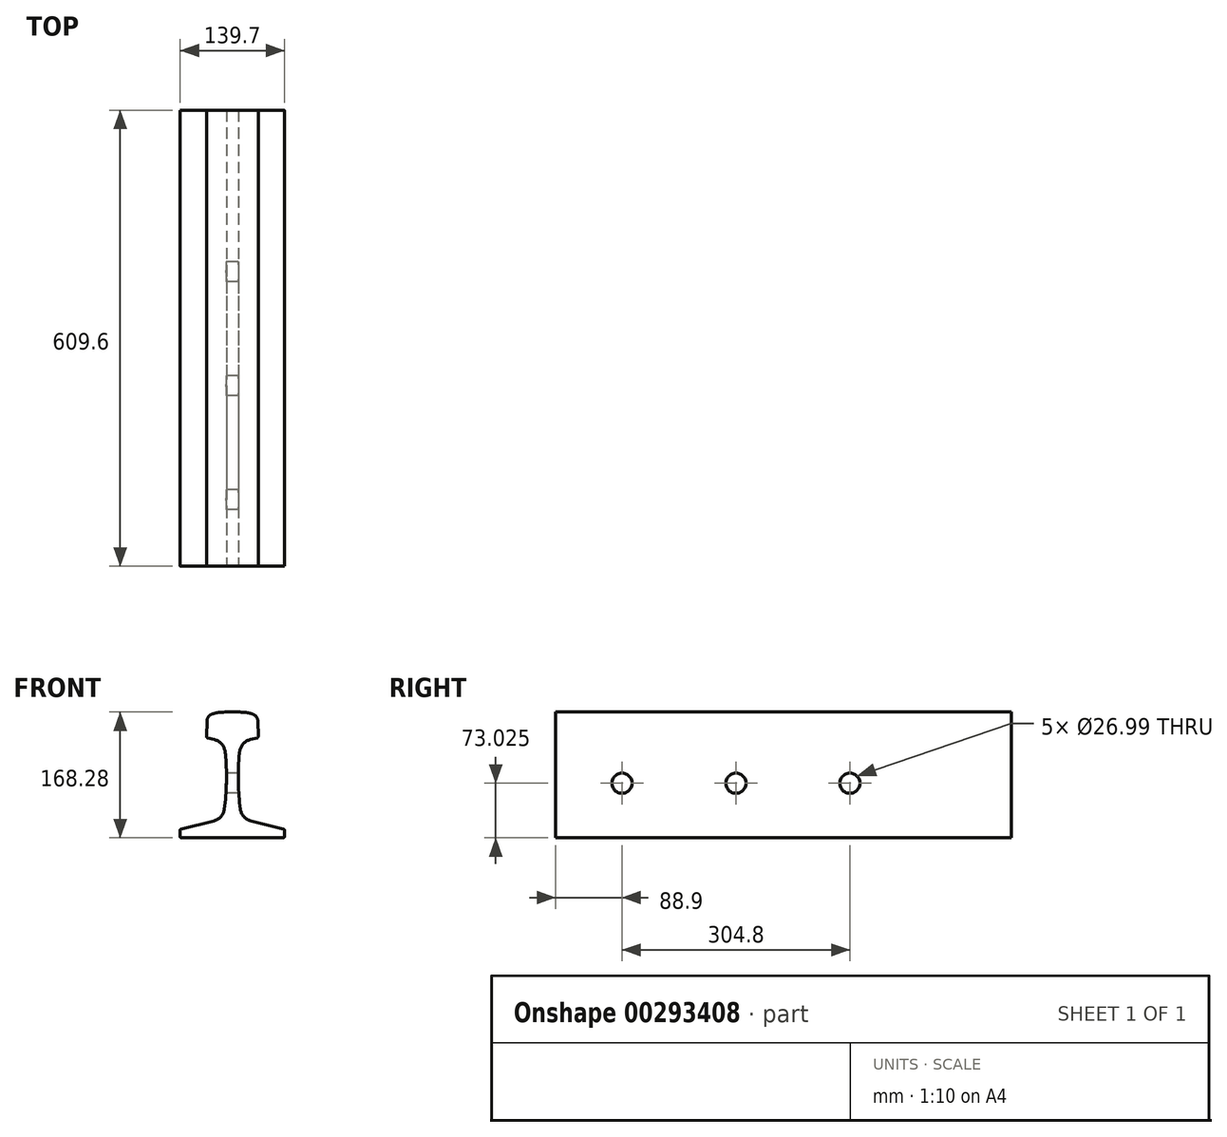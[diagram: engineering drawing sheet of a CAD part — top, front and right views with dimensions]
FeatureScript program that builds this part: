
annotation { "Feature Type Name" : "Feature", "Feature Type Description" : "" }
export const myFeature = defineFeature(function(context is Context, id is Id, definition is map)
    precondition{}
    {
        {
            var Q0;
            Q0=qCreatedBy(makeId("Front.planeOp"),FACE);
            var sketch = newSketch(context, id + "F0", { "sketchPlane" : qUnion([Q0])});
            skLineSegment(sketch, "E0", {"start": v(0, 192.8) * mm, "end": v(0, -23.67) * mm, "construction": true});
            skLineSegment(sketch, "E1", {"start": v(0, 0) * mm, "end": v(68.26, 0) * mm});
            skLineSegment(sketch, "E2", {"start": v(69.85, 1.59) * mm, "end": v(69.85, 9.92) * mm});
            skLineSegment(sketch, "E3", {"start": v(68.65, 11.46) * mm, "end": v(24.97, 22.35) * mm});
            skArc(sketch, "E4", {"start": v(68.26, 0) * mm, "mid": v(69.39, 0.46) * mm, "end": v(69.85, 1.59) * mm});
            skArc(sketch, "E5", {"start": v(69.85, 9.92) * mm, "mid": v(69.51, 10.9) * mm, "end": v(68.65, 11.46) * mm});
            skArc(sketch, "E6", {"start": v(10.68, 38.47) * mm, "mid": v(15.33, 28.2) * mm, "end": v(24.97, 22.35) * mm});
            skArc(sketch, "E7", {"start": v(7.94, 82.55) * mm, "mid": v(8.62, 60.47) * mm, "end": v(10.68, 38.47) * mm});
            skArc(sketch, "E8", {"start": v(8.85, 107.95) * mm, "mid": v(8.16, 95.26) * mm, "end": v(7.94, 82.55) * mm});
            skLineSegment(sketch, "E9", {"start": v(-374.2, 82.55) * mm, "end": v(-11.1, 82.55) * mm, "construction": true});
            skArc(sketch, "E10", {"start": v(9.93, 116.4) * mm, "mid": v(9.27, 112.19) * mm, "end": v(8.85, 107.95) * mm});
            skLineSegment(sketch, "E11", {"start": v(-63.11, 125.41) * mm, "end": v(54.14, 125.41) * mm, "construction": true});
            skArc(sketch, "E12", {"start": v(15.87, 167.78) * mm, "mid": v(7.94, 168.15) * mm, "end": v(0, 168.28) * mm});
            skArc(sketch, "E13", {"start": v(28.14, 164.93) * mm, "mid": v(22.13, 166.86) * mm, "end": v(15.87, 167.78) * mm});
            skArc(sketch, "E14", {"start": v(34, 156.37) * mm, "mid": v(32.34, 161.52) * mm, "end": v(28.14, 164.93) * mm});
            skArc(sketch, "E15", {"start": v(33.32, 133.72) * mm, "mid": v(34.2, 134.3) * mm, "end": v(34.53, 135.3) * mm});
            skLineSegment(sketch, "E16", {"start": v(34, 156.37) * mm, "end": v(34.53, 135.3) * mm});
            skArc(sketch, "E17", {"start": v(24.05, 131.4) * mm, "mid": v(14.78, 125.98) * mm, "end": v(9.93, 116.4) * mm});
            skLineSegment(sketch, "E18", {"start": v(24.05, 131.4) * mm, "end": v(33.32, 133.72) * mm});
            skLineSegment(sketch, "E19", {"start": v(34.53, 172.82) * mm, "end": v(34.53, 129.5) * mm, "construction": true});
            skArc(sketch, "E20.MirrorCS", {"start": v(-68.26, 0) * mm, "mid": v(-69.39, 0.46) * mm, "end": v(-69.85, 1.59) * mm});
            skLineSegment(sketch, "E21.MirrorCS", {"start": v(0, 0) * mm, "end": v(-68.26, 0) * mm});
            skLineSegment(sketch, "E22.MirrorCS", {"start": v(-69.85, 1.59) * mm, "end": v(-69.85, 9.92) * mm});
            skArc(sketch, "E23.MirrorCS", {"start": v(-69.85, 9.92) * mm, "mid": v(-69.51, 10.9) * mm, "end": v(-68.65, 11.46) * mm});
            skLineSegment(sketch, "E24.MirrorCS", {"start": v(-68.65, 11.46) * mm, "end": v(-24.97, 22.35) * mm});
            skArc(sketch, "E25.MirrorCS", {"start": v(-10.68, 38.47) * mm, "mid": v(-15.33, 28.2) * mm, "end": v(-24.97, 22.35) * mm});
            skArc(sketch, "E26.MirrorCS", {"start": v(-7.94, 82.55) * mm, "mid": v(-8.62, 60.47) * mm, "end": v(-10.68, 38.47) * mm});
            skArc(sketch, "E27.MirrorCS", {"start": v(-8.85, 107.95) * mm, "mid": v(-8.16, 95.26) * mm, "end": v(-7.94, 82.55) * mm});
            skArc(sketch, "E28.MirrorCS", {"start": v(-9.93, 116.4) * mm, "mid": v(-9.27, 112.19) * mm, "end": v(-8.85, 107.95) * mm});
            skArc(sketch, "E29.MirrorCS", {"start": v(-24.05, 131.4) * mm, "mid": v(-14.78, 125.98) * mm, "end": v(-9.93, 116.4) * mm});
            skLineSegment(sketch, "E30.MirrorCS", {"start": v(-34, 156.37) * mm, "end": v(-34.53, 135.3) * mm});
            skLineSegment(sketch, "E31.MirrorCS", {"start": v(-24.05, 131.4) * mm, "end": v(-33.32, 133.72) * mm});
            skArc(sketch, "E32.MirrorCS", {"start": v(-33.32, 133.72) * mm, "mid": v(-34.2, 134.3) * mm, "end": v(-34.53, 135.3) * mm});
            skArc(sketch, "E33.MirrorCS", {"start": v(-34, 156.37) * mm, "mid": v(-32.34, 161.52) * mm, "end": v(-28.14, 164.93) * mm});
            skArc(sketch, "E34.MirrorCS", {"start": v(-28.14, 164.93) * mm, "mid": v(-22.13, 166.86) * mm, "end": v(-15.87, 167.78) * mm});
            skArc(sketch, "E35.MirrorCS", {"start": v(-15.88, 167.78) * mm, "mid": v(-7.94, 168.15) * mm, "end": v(0, 168.28) * mm});
            skLineSegment(sketch, "E36", {"start": v(0, 28.57) * mm, "end": v(-68.65, 11.46) * mm, "construction": true});
            skLineSegment(sketch, "E37", {"start": v(-54.52, 28.57) * mm, "end": v(0, 28.57) * mm, "construction": true});
            skLineSegment(sketch, "E38", {"start": v(-34.53, 173.1) * mm, "end": v(-34.53, 129.66) * mm, "construction": true});
            skLineSegment(sketch, "E39", {"start": v(0, 125.41) * mm, "end": v(-57.31, 139.7) * mm, "construction": true});
            skLineSegment(sketch, "E40", {"start": v(-24.48, 73.03) * mm, "end": v(98.37, 73.03) * mm, "construction": true});
            skPoint(sketch, "E41", {"position": v(8.07, 73.03) * mm});
            skPoint(sketch, "E42", {"position": v(-8.07, 73.03) * mm});
            skSolve(sketch);
        }
        {
            var Q0;
            Q0=makeQuery(id+"F0.imprint","IMPRINT",FACE,{"disambiguationData":[TD([[makeQuery(id+"F0.imprint","IMPRINT",EDGE,{"derivedFrom":sQuery(id+"F0.wireOp",EDGE,"E1")}),1.0]])]});
            extrude(context, id + "F1", {"entities" : qUnion([Q0]), "oppositeDirection" : true, "depth" : 609.6 * mm});
        }
        {
            var Q0;
            Q0=qCreatedBy(makeId("Right.planeOp"),FACE);
            cPlane(context, id + "F2", {"entities" : qUnion([Q0]), "cplaneType" : CPlaneType.OFFSET, "offset" : 76.2 * mm, "width" : 152.4 * mm, "height" : 152.4 * mm});
        }
        {
            var Q0;
            Q0=qCreatedBy(id+"F2.planeOp",FACE);
            var sketch = newSketch(context, id + "F3", { "sketchPlane" : qUnion([Q0])});
            skPoint(sketch, "E43", {"position": v(88.9, 73.02) * mm});
            skPoint(sketch, "E44", {"position": v(241.3, 73.03) * mm});
            skPoint(sketch, "E45", {"position": v(393.7, 73.03) * mm});
            skLineSegment(sketch, "E46", {"start": v(-1.59, 181.23) * mm, "end": v(-1.59, -28.23) * mm, "construction": true});
            skPoint(sketch, "E47.MirrorP", {"position": v(-396.88, 73.02) * mm});
            skPoint(sketch, "E48.MirrorP", {"position": v(-244.48, 73.02) * mm});
            skPoint(sketch, "E49.MirrorP", {"position": v(-92.08, 73.02) * mm});
            skSolve(sketch);
        }
        {
            var Q0;
            Q0=makeQuery(id+"F0.imprint","IMPRINT",FACE,{"disambiguationData":[TD([[makeQuery(id+"F0.imprint","IMPRINT",EDGE,{"derivedFrom":sQuery(id+"F0.wireOp",EDGE,"E1")}),1.0]])]});
            extrude(context, id + "F4", {"entities" : qUnion([Q0]), "oppositeDirection" : true, "depth" : 609.6 * mm});
        }
        {
            var Q0;
            Q0=sQuery(id+"F3.wireOp",VERTEX,"E43");
            var Q1;
            Q1=sQuery(id+"F3.wireOp",VERTEX,"E44");
            var Q2;
            Q2=makeQuery(id+"F4.opExtrude","SWEPT_BODY",BODY,{"disambiguationData":[OSD([sQuery(id+"F0.wireOp",EDGE,"E1"),sQuery(id+"F0.wireOp",EDGE,"E2"),sQuery(id+"F0.wireOp",EDGE,"E3"),sQuery(id+"F0.wireOp",EDGE,"E4"),sQuery(id+"F0.wireOp",EDGE,"E5"),sQuery(id+"F0.wireOp",EDGE,"E6"),sQuery(id+"F0.wireOp",EDGE,"E7"),sQuery(id+"F0.wireOp",EDGE,"E8"),sQuery(id+"F0.wireOp",EDGE,"E10"),sQuery(id+"F0.wireOp",EDGE,"E12"),sQuery(id+"F0.wireOp",EDGE,"E13"),sQuery(id+"F0.wireOp",EDGE,"E14"),sQuery(id+"F0.wireOp",EDGE,"E15"),sQuery(id+"F0.wireOp",EDGE,"E16"),sQuery(id+"F0.wireOp",EDGE,"E17"),sQuery(id+"F0.wireOp",EDGE,"E18"),sQuery(id+"F0.wireOp",EDGE,"E20.MirrorCS"),sQuery(id+"F0.wireOp",EDGE,"E21.MirrorCS"),sQuery(id+"F0.wireOp",EDGE,"E22.MirrorCS"),sQuery(id+"F0.wireOp",EDGE,"E23.MirrorCS"),sQuery(id+"F0.wireOp",EDGE,"E24.MirrorCS"),sQuery(id+"F0.wireOp",EDGE,"E25.MirrorCS"),sQuery(id+"F0.wireOp",EDGE,"E26.MirrorCS"),sQuery(id+"F0.wireOp",EDGE,"E27.MirrorCS"),sQuery(id+"F0.wireOp",EDGE,"E28.MirrorCS"),sQuery(id+"F0.wireOp",EDGE,"E29.MirrorCS"),sQuery(id+"F0.wireOp",EDGE,"E30.MirrorCS"),sQuery(id+"F0.wireOp",EDGE,"E31.MirrorCS"),sQuery(id+"F0.wireOp",EDGE,"E32.MirrorCS"),sQuery(id+"F0.wireOp",EDGE,"E33.MirrorCS"),sQuery(id+"F0.wireOp",EDGE,"E34.MirrorCS"),sQuery(id+"F0.wireOp",EDGE,"E35.MirrorCS")])]});
            hole(context, id + "F5", {"style" : HoleStyle.SIMPLE, "endStyle" : HoleEndStyle.THROUGH, "holeDiameter" : 26.99 * mm, "startFromSketch" : true, "locations" : qUnion([Q0, Q1]), "scope" : qUnion([Q2]), "isTappedThrough" : true});
        }
        {
            var Q0;
            Q0=makeQuery(id+"F0.imprint","IMPRINT",FACE,{"disambiguationData":[TD([[makeQuery(id+"F0.imprint","IMPRINT",EDGE,{"derivedFrom":sQuery(id+"F0.wireOp",EDGE,"E1")}),1.0]])]});
            extrude(context, id + "F6", {"entities" : qUnion([Q0]), "oppositeDirection" : true, "depth" : 609.6 * mm});
        }
        {
            var Q0;
            Q0=sQuery(id+"F3.wireOp",VERTEX,"E43");
            var Q1;
            Q1=sQuery(id+"F3.wireOp",VERTEX,"E44");
            var Q2;
            Q2=sQuery(id+"F3.wireOp",VERTEX,"E45");
            var Q3;
            Q3=makeQuery(id+"F6.opExtrude","SWEPT_BODY",BODY,{"disambiguationData":[OSD([sQuery(id+"F0.wireOp",EDGE,"E1"),sQuery(id+"F0.wireOp",EDGE,"E2"),sQuery(id+"F0.wireOp",EDGE,"E3"),sQuery(id+"F0.wireOp",EDGE,"E4"),sQuery(id+"F0.wireOp",EDGE,"E5"),sQuery(id+"F0.wireOp",EDGE,"E6"),sQuery(id+"F0.wireOp",EDGE,"E7"),sQuery(id+"F0.wireOp",EDGE,"E8"),sQuery(id+"F0.wireOp",EDGE,"E10"),sQuery(id+"F0.wireOp",EDGE,"E12"),sQuery(id+"F0.wireOp",EDGE,"E13"),sQuery(id+"F0.wireOp",EDGE,"E14"),sQuery(id+"F0.wireOp",EDGE,"E15"),sQuery(id+"F0.wireOp",EDGE,"E16"),sQuery(id+"F0.wireOp",EDGE,"E17"),sQuery(id+"F0.wireOp",EDGE,"E18"),sQuery(id+"F0.wireOp",EDGE,"E20.MirrorCS"),sQuery(id+"F0.wireOp",EDGE,"E21.MirrorCS"),sQuery(id+"F0.wireOp",EDGE,"E22.MirrorCS"),sQuery(id+"F0.wireOp",EDGE,"E23.MirrorCS"),sQuery(id+"F0.wireOp",EDGE,"E24.MirrorCS"),sQuery(id+"F0.wireOp",EDGE,"E25.MirrorCS"),sQuery(id+"F0.wireOp",EDGE,"E26.MirrorCS"),sQuery(id+"F0.wireOp",EDGE,"E27.MirrorCS"),sQuery(id+"F0.wireOp",EDGE,"E28.MirrorCS"),sQuery(id+"F0.wireOp",EDGE,"E29.MirrorCS"),sQuery(id+"F0.wireOp",EDGE,"E30.MirrorCS"),sQuery(id+"F0.wireOp",EDGE,"E31.MirrorCS"),sQuery(id+"F0.wireOp",EDGE,"E32.MirrorCS"),sQuery(id+"F0.wireOp",EDGE,"E33.MirrorCS"),sQuery(id+"F0.wireOp",EDGE,"E34.MirrorCS"),sQuery(id+"F0.wireOp",EDGE,"E35.MirrorCS")])]});
            hole(context, id + "F7", {"style" : HoleStyle.SIMPLE, "endStyle" : HoleEndStyle.THROUGH, "holeDiameter" : 26.99 * mm, "startFromSketch" : true, "locations" : qUnion([Q0, Q1, Q2]), "scope" : qUnion([Q3]), "isTappedThrough" : true});
        }
    });
